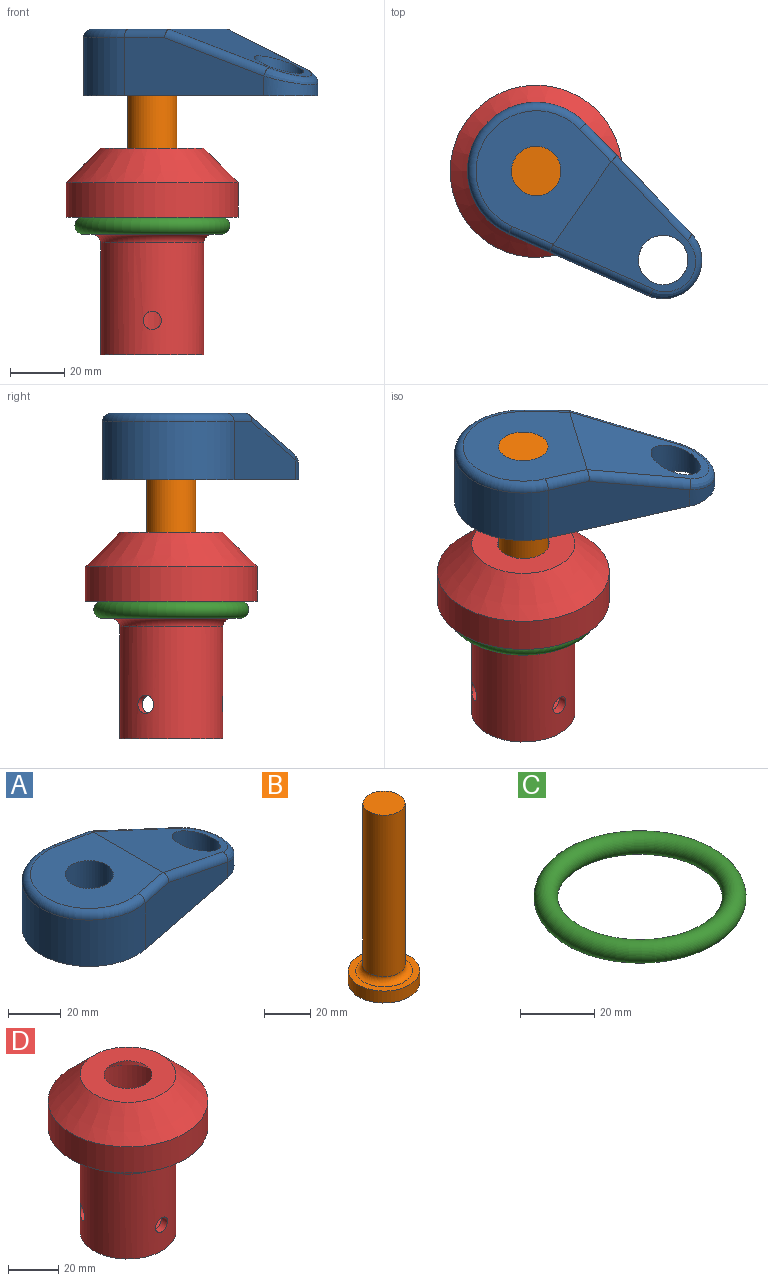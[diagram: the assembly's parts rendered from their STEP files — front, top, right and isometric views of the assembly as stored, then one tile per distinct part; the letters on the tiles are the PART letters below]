
ASSEMBLY  parts=4 mates=3
PART A: 15 faces, bbox 98.9x55x24.6 mm
  f0: plane 54.99x21.43mm, normal (0.19,0.98,0), area 919.6mm2, adj f2,f4,f5,f13,f14
  f1: plane 54.99x21.43mm, normal (0.19,-0.98,0), area 919.6mm2, adj f2,f4,f5,f9,f10
  f2: cylinder r=14.29mm len=28.03mm, axis (0,0,1), area 206.8mm2, adj f0,f1,f4,f12
  f3: cylinder r=9.13mm len=18.26mm, axis (0,0,1), area 658.7mm2, adj f4,f8
  f4: plane 96.84x50.8mm, normal (0,0,-1), area 3121.7mm2, adj f0,f1,f2,f3,f5,f7
  f5: cylinder r=25.4mm len=50.8mm, axis (0,0,1), area 1923.2mm2, adj f0,f1,f4,f11
  f6: plane 44.45x42.86mm, normal (0,0,1), area 1363.6mm2, adj f7,f8,f9,f11,f13
  f7: cylinder r=9.13mm len=24.61mm, axis (0,0,1), area 1411.3mm2, adj f4,f6
  f8: plane 48.71x37.56mm, normal (0.34,0,0.94), area 1130.8mm2, adj f3,f6,f9,f10,f12,f13,f14
  f9: cylinder r=3.17mm len=16.93mm, axis (0.98,0.19,0), area 81.9mm2, adj f1,f6,f8,f10,f11
  f10: cylinder r=3.17mm len=40.32mm, axis (-0.93,-0.18,0.33), area 204.2mm2, adj f1,f8,f9,f12
  f11: torus R=22.23mm, axis (0,0,1), area 427.2mm2, adj f5,f6,f9,f13
  f12: bspline ~28.03x11.51mm, area 153.5mm2, adj f2,f8,f10,f14
  f13: cylinder r=3.17mm len=16.93mm, axis (-0.98,0.19,0), area 81.9mm2, adj f0,f6,f8,f11,f14
  f14: cylinder r=3.17mm len=40.32mm, axis (0.93,-0.18,-0.33), area 204.2mm2, adj f0,f8,f12,f13
PART B: 6 faces, bbox 31x31x95.3 mm
  f0: plane 30.96x30.96mm, normal (0,0,-1), area 752.6mm2, adj f1
  f1: cylinder r=15.48mm len=30.96mm, axis (0,0,-1), area 617.5mm2, adj f0,f2
  f2: plane 30.96x30.96mm, normal (0,0,1), area 277.1mm2, adj f1,f5
  f3: cylinder r=9.13mm len=85.73mm, axis (0,0,-1), area 4916.6mm2, adj f4,f5
  f4: plane 18.26x18.26mm, normal (0,0,1), area 261.8mm2, adj f3
  f5: torus R=12.3mm, axis (0,0,-1), area 322.2mm2, adj f2,f3
PART C: 1 faces, bbox 61.9x61.9x6.4 mm
  f0: torus R=25.4mm, axis (0,0,1), area 3183.7mm2
PART D: 17 faces, bbox 63.5x63.5x76.2 mm
  f0: cylinder r=19.05mm len=41.28mm, axis (0,0,-1), area 4832.2mm2, adj f2,f10,f11,f12,f13
  f1: cylinder r=15.88mm len=63.5mm, axis (0,0,-1), area 6225.5mm2, adj f8,f9,f10,f11,f12
  f2: plane 38.1x38.1mm, normal (0,0,-1), area 855.1mm2, adj f0,f16
  f3: cylinder r=22.23mm len=44.45mm, axis (0,0,-1), area 443.4mm2, adj f13,f14
  f4: plane 63.5x63.5mm, normal (0,0,-1), area 1140.1mm2, adj f5,f14
  f5: cylinder r=31.75mm len=63.5mm, axis (0,0,-1), area 2533.5mm2, adj f4,f6
  f6: cone r=19.05mm half-angle=45deg, axis (0,0,-1), area 2866.4mm2, adj f5,f7
  f7: plane 38.1x38.1mm, normal (0,0,1), area 855.1mm2, adj f6,f8
  f8: cone r=9.53mm half-angle=45deg, axis (0,0,-1), area 716.6mm2, adj f1,f7
  f9: plane 31.75x31.75mm, normal (0,0,1), area 665.1mm2, adj f1,f15
  f10: cylinder r=3.38mm len=6.76mm, axis (0,1,0), area 68mm2, adj f0,f1
  f11: cylinder r=3.38mm len=7.62mm, axis (-0.87,-0.5,0), area 68mm2, adj f0,f1
  f12: cylinder r=3.38mm len=7.62mm, axis (0.87,-0.5,0), area 68mm2, adj f0,f1
  f13: torus R=22.23mm, axis (0,0,1), area 633.1mm2, adj f0,f3
  f14: torus R=25.4mm, axis (0,0,1), area 732.6mm2, adj f3,f4
  f15: cylinder r=6.35mm len=12.7mm, axis (0,0,-1), area 126.7mm2, adj f9,f16
  f16: cone r=6.35mm half-angle=45deg, axis (0,0,-1), area 223.9mm2, adj f2,f15
PLACE A rot(axis=(0,0,-1),35deg) t=(0,0,18.54)mm
PLACE B rot(axis=(0,0,-1),35deg) t=(0,0,18.54)mm
PLACE C t=(0,0,47.63)mm
PLACE D at identity fixed
MATE cylindrical B.f1 <-> D.f0  axis (0,0,-1) through (0,0,24.89)mm
MATE fastened C.f0 <-> D.f0  axis (0,0,1) through (0,0,47.63)mm
MATE fastened B.f1 <-> A.f5  axis (0,0,-1) through (0,0,120.14)mm
